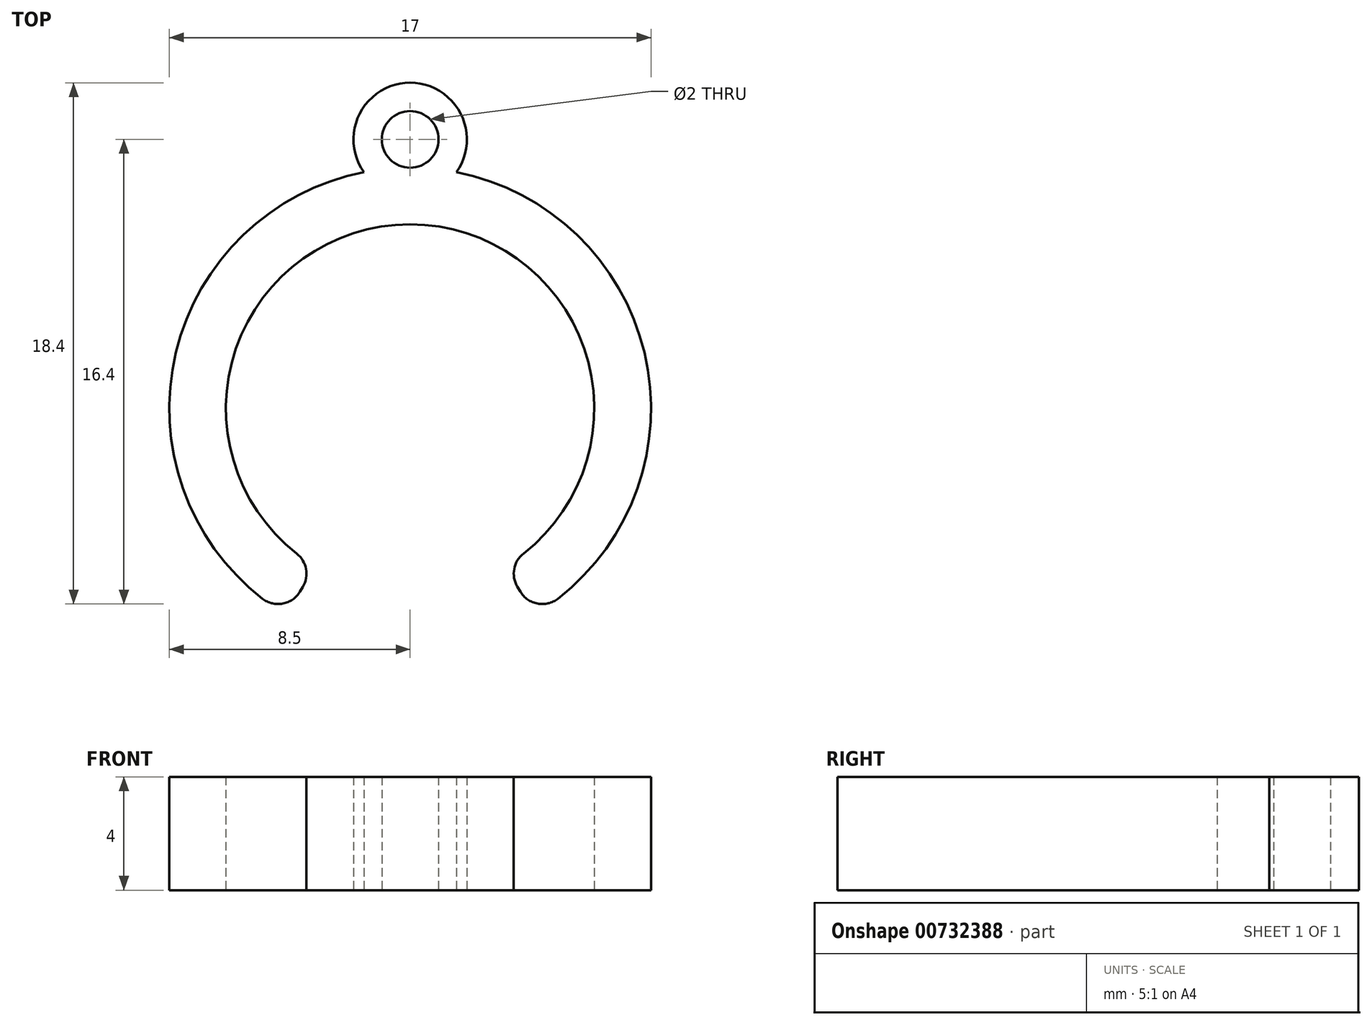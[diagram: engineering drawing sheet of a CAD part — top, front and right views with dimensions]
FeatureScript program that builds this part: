
annotation { "Feature Type Name" : "Feature", "Feature Type Description" : "" }
export const myFeature = defineFeature(function(context is Context, id is Id, definition is map)
    precondition{}
    {
        {
            var Q0;
            Q0=qCreatedBy(makeId("Top.planeOp"),FACE);
            var sketch = newSketch(context, id + "F0", { "sketchPlane" : qUnion([Q0])});
            skCircle(sketch, "E0", {"center": v(0, 0) * mm, "radius": 6.5 * mm});
            skCircle(sketch, "E1", {"center": v(0, 0) * mm, "radius": 8.5 * mm});
            skCircle(sketch, "E2", {"center": v(0, 9.5) * mm, "radius": 2 * mm});
            skCircle(sketch, "E3", {"center": v(0, 9.5) * mm, "radius": 1 * mm});
            skLineSegment(sketch, "E4", {"start": v(0, 0) * mm, "end": v(-5.09, -8.46) * mm});
            skLineSegment(sketch, "E5", {"start": v(0.02, -0.03) * mm, "end": v(5.1, -8.49) * mm});
            skSolve(sketch);
        }
        {
            var Q0;
            {var subQ0=sQuery(id+"F0.wireOp",EDGE,"E3");Q0=makeQuery(id+"F0.imprint","IMPRINT",FACE,{"disambiguationData":[TD([[makeQuery(id+"F0.imprint","IMPRINT",EDGE,{"derivedFrom":subQ0}),-1.0]])]});}
            var Q1;
            {var subQ0=sQuery(id+"F0.wireOp",EDGE,"E1");var subQ1=makeQuery(id+"F0.imprint","INTERSECT",VERTEX,{"derivedFrom":[subQ0,sQuery(id+"F0.wireOp",EDGE,"E3")]});Q1=makeQuery(id+"F0.imprint","IMPRINT",FACE,{"disambiguationData":[TD([[makeQuery(id+"F0.imprint","IMPRINT",EDGE,{"disambiguationData":[TD([[subQ1,1.0]])],"derivedFrom":subQ0}),1.0]])]});}
            var Q2;
            {var subQ4=sQuery(id+"F0.wireOp",EDGE,"E4");var subQ8=sQuery(id+"F0.wireOp",EDGE,"E0");var subQ9=makeQuery(id+"F0.imprint","INTERSECT",VERTEX,{"derivedFrom":[subQ8,subQ4]});Q2=makeQuery(id+"F0.imprint","IMPRINT",FACE,{"disambiguationData":[TD([[makeQuery(id+"F0.imprint","IMPRINT",EDGE,{"disambiguationData":[TD([[subQ9,1.0]])],"derivedFrom":subQ8}),-1.0]])]});}
            extrude(context, id + "F1", {"entities" : qUnion([Q0, Q1, Q2]), "depth" : 4 * mm, "offsetDistance" : 25 * mm});
        }
        {
            var Q0;
            Q0=makeQuery(id+"F1.opExtrude","SWEPT_EDGE",EDGE,{"disambiguationData":[OSD([sQuery(id+"F0.wireOp",EDGE,"E1"),sQuery(id+"F0.wireOp",EDGE,"E5")])]});
            var Q1;
            Q1=makeQuery(id+"F1.opExtrude","SWEPT_EDGE",EDGE,{"disambiguationData":[OSD([sQuery(id+"F0.wireOp",EDGE,"E0"),sQuery(id+"F0.wireOp",EDGE,"E5")])]});
            var Q2;
            Q2=makeQuery(id+"F1.opExtrude","SWEPT_EDGE",EDGE,{"disambiguationData":[OSD([sQuery(id+"F0.wireOp",EDGE,"E0"),sQuery(id+"F0.wireOp",EDGE,"E4")])]});
            var Q3;
            Q3=makeQuery(id+"F1.opExtrude","SWEPT_EDGE",EDGE,{"disambiguationData":[OSD([sQuery(id+"F0.wireOp",EDGE,"E1"),sQuery(id+"F0.wireOp",EDGE,"E4")])]});
            fillet(context, id + "F2", {"entities" : qUnion([Q0, Q1, Q2, Q3]), "radius" : 0.9 * mm, "tangentPropagation" : true, "allowEdgeOverflow" : false});
        }
    });
